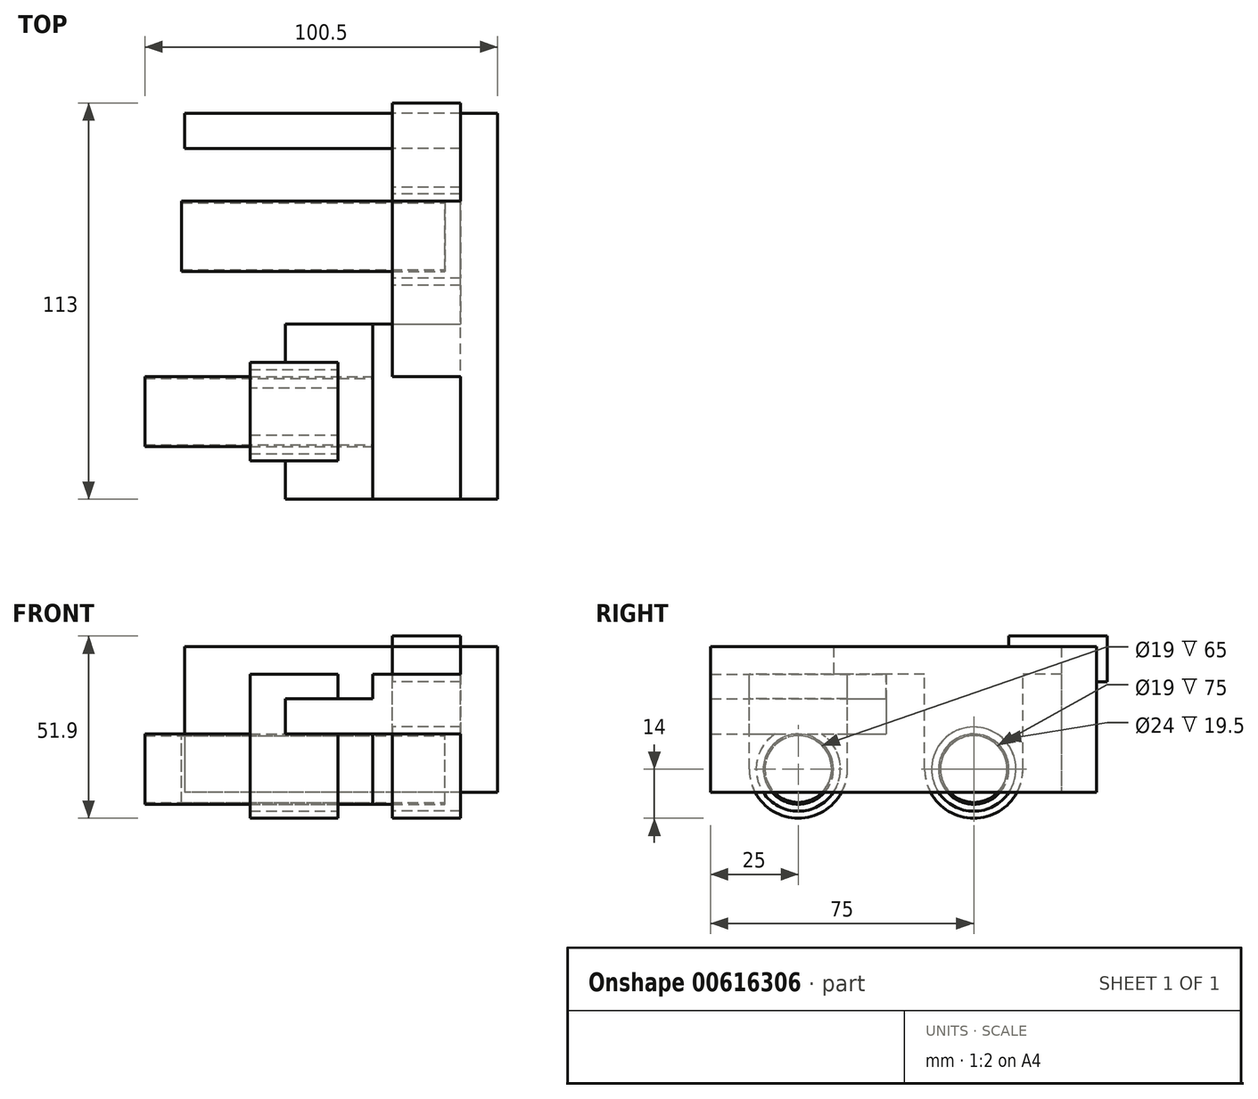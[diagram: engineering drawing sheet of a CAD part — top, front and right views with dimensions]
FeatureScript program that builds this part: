
annotation { "Feature Type Name" : "Feature", "Feature Type Description" : "" }
export const myFeature = defineFeature(function(context is Context, id is Id, definition is map)
    precondition{}
    {
        {
            var Q0;
            Q0=qCreatedBy(makeId("Front.planeOp"),FACE);
            var sketch = newSketch(context, id + "F0", { "sketchPlane" : qUnion([Q0])});
            skLineSegment(sketch, "E0.bottom", {"start": v(-30.5, 5.1) * mm, "end": v(30, 5.1) * mm});
            skLineSegment(sketch, "E0.top", {"start": v(-30.5, -5) * mm, "end": v(30, -5) * mm});
            skLineSegment(sketch, "E0.left", {"start": v(-30.5, 5.1) * mm, "end": v(-30.5, -5) * mm});
            skPoint(sketch, "E0.middle", {"position": v(0, 0) * mm});
            skLineSegment(sketch, "E1.bottom", {"start": v(-5.5, 5.1) * mm, "end": v(30, 5.1) * mm});
            skLineSegment(sketch, "E1.top", {"start": v(-5.5, 12.1) * mm, "end": v(30, 12.1) * mm});
            skLineSegment(sketch, "E1.left", {"start": v(-5.5, 5.1) * mm, "end": v(-5.5, 12.1) * mm});
            skLineSegment(sketch, "E2", {"start": v(19.5, 5.1) * mm, "end": v(19.5, 12.1) * mm});
            skLineSegment(sketch, "E3", {"start": v(30, -5) * mm, "end": v(30, 19.9) * mm});
            skLineSegment(sketch, "E4", {"start": v(30, 19.9) * mm, "end": v(19.5, 19.9) * mm});
            skLineSegment(sketch, "E5", {"start": v(19.5, 19.9) * mm, "end": v(19.5, -5) * mm});
            skLineSegment(sketch, "E6.bottom", {"start": v(19.5, -5) * mm, "end": v(30, -5) * mm});
            skLineSegment(sketch, "E6.top", {"start": v(19.5, -21.67) * mm, "end": v(30, -21.67) * mm});
            skLineSegment(sketch, "E6.left", {"start": v(19.5, -5) * mm, "end": v(19.5, -21.67) * mm});
            skLineSegment(sketch, "E6.right", {"start": v(30, -5) * mm, "end": v(30, -21.67) * mm});
            skSolve(sketch);
        }
        {
            var Q0;
            {var subQ0=sQuery(id+"F0.wireOp",EDGE,"E0.left");var subQ5=sQuery(id+"F0.wireOp",EDGE,"E2");var subQ6=sQuery(id+"F0.wireOp",EDGE,"E0.bottom");var subQ9=sQuery(id+"F0.wireOp",EDGE,"E1.left");var subQ12=sQuery(id+"F0.wireOp",EDGE,"E3");var subQ13=makeQuery(id+"F0.imprint","INTERSECT",VERTEX,{"derivedFrom":[subQ6,subQ12]});var subQ14=makeQuery(id+"F0.imprint","IMPRINT",EDGE,{"disambiguationData":[TD([[subQ13,1.0]])],"derivedFrom":subQ6});var subQ19=makeQuery(id+"F0.imprint","IMPRINT",EDGE,{"derivedFrom":subQ5});var subQ20=sQuery(id+"F0.wireOp",EDGE,"E4");Q0=qUnion([makeQuery(id+"F0.imprint","IMPRINT",FACE,{"disambiguationData":[TD([[makeQuery(id+"F0.imprint","IMPRINT",EDGE,{"derivedFrom":subQ9}),-1.0]])]}),makeQuery(id+"F0.imprint","IMPRINT",FACE,{"disambiguationData":[TD([[makeQuery(id+"F0.imprint","IMPRINT",EDGE,{"derivedFrom":sQuery(id+"F0.wireOp",EDGE,"E6.top")}),1.0]])]}),makeQuery(id+"F0.imprint","IMPRINT",FACE,{"disambiguationData":[TD([[subQ14,-1.0]])]}),makeQuery(id+"F0.imprint","IMPRINT",FACE,{"disambiguationData":[TD([[makeQuery(id+"F0.imprint","IMPRINT",EDGE,{"derivedFrom":subQ20}),1.0]])]}),makeQuery(id+"F0.imprint","IMPRINT",FACE,{"disambiguationData":[TD([[subQ19,-1.0]])]}),makeQuery(id+"F0.imprint","IMPRINT",FACE,{"disambiguationData":[TD([[makeQuery(id+"F0.imprint","IMPRINT",EDGE,{"derivedFrom":subQ0}),1.0]])]})]);}
            extrude(context, id + "F1", {"entities" : qUnion([Q0]), "depth" : 25 * mm, "offsetDistance" : 25 * mm, "hasSecondDirection" : true, "secondDirectionOppositeDirection" : true, "secondDirectionDepth" : 25 * mm});
        }
        {
            var Q0;
            Q0=makeQuery(id+"F1.opExtrude","CAP_FACE",FACE,{"disambiguationData":[OSD([sQuery(id+"F0.wireOp",EDGE,"E0.bottom"),sQuery(id+"F0.wireOp",EDGE,"E0.top"),sQuery(id+"F0.wireOp",EDGE,"E0.left"),sQuery(id+"F0.wireOp",EDGE,"E1.top"),sQuery(id+"F0.wireOp",EDGE,"E1.left"),sQuery(id+"F0.wireOp",EDGE,"E3"),sQuery(id+"F0.wireOp",EDGE,"E4"),sQuery(id+"F0.wireOp",EDGE,"E5"),sQuery(id+"F0.wireOp",EDGE,"E6.top"),sQuery(id+"F0.wireOp",EDGE,"E6.left"),sQuery(id+"F0.wireOp",EDGE,"E6.right")])],"isStart":true});
            var sketch = newSketch(context, id + "F2", { "sketchPlane" : qUnion([Q0])});
            skLineSegment(sketch, "E7.0.0", {"start": v(-19.5, 12.1) * mm, "end": v(-19.5, 19.9) * mm, "construction": true});
            skLineSegment(sketch, "E7.0.1", {"start": v(-19.5, 19.9) * mm, "end": v(-30, 19.9) * mm, "construction": true});
            skLineSegment(sketch, "E7.0.2", {"start": v(-30, 19.9) * mm, "end": v(-30, -21.67) * mm, "construction": true});
            skLineSegment(sketch, "E7.0.3", {"start": v(-30, -21.67) * mm, "end": v(-19.5, -21.67) * mm, "construction": true});
            skLineSegment(sketch, "E7.0.4", {"start": v(-19.5, -21.67) * mm, "end": v(-19.5, -5) * mm, "construction": true});
            skLineSegment(sketch, "E7.0.5", {"start": v(-19.5, -5) * mm, "end": v(30.5, -5) * mm, "construction": true});
            skLineSegment(sketch, "E7.0.6", {"start": v(30.5, -5) * mm, "end": v(30.5, 5.1) * mm, "construction": true});
            skLineSegment(sketch, "E7.0.7", {"start": v(30.5, 5.1) * mm, "end": v(5.5, 5.1) * mm, "construction": true});
            skLineSegment(sketch, "E7.0.8", {"start": v(5.5, 5.1) * mm, "end": v(5.5, 12.1) * mm, "construction": true});
            skLineSegment(sketch, "E7.0.9", {"start": v(5.5, 12.1) * mm, "end": v(-19.5, 12.1) * mm, "construction": true});
            skLineSegment(sketch, "E8.bottom", {"start": v(-30, 19.9) * mm, "end": v(-19.5, 19.9) * mm});
            skLineSegment(sketch, "E8.top", {"start": v(-30, -21.67) * mm, "end": v(-19.5, -21.67) * mm});
            skLineSegment(sketch, "E8.left", {"start": v(-30, 19.9) * mm, "end": v(-30, -21.67) * mm});
            skLineSegment(sketch, "E8.right", {"start": v(-19.5, 19.9) * mm, "end": v(-19.5, -21.67) * mm});
            skSolve(sketch);
        }
        {
            var Q0;
            Q0 = qSketchRegion(id + "F2", true);
            extrude(context, id + "F3", {"entities" : qUnion([Q0]), "operationType" : NewBodyOperationType.ADD, "depth" : 50 * mm, "offsetDistance" : 25 * mm});
        }
        {
            var Q0;
            Q0=makeQuery(id+"F3.opExtrude","CAP_FACE",FACE,{"disambiguationData":[OSD([sQuery(id+"F2.wireOp",EDGE,"E8.bottom"),sQuery(id+"F2.wireOp",EDGE,"E8.top"),sQuery(id+"F2.wireOp",EDGE,"E8.left"),sQuery(id+"F2.wireOp",EDGE,"E8.right")])],"isStart":false});
            var sketch = newSketch(context, id + "F4", { "sketchPlane" : qUnion([Q0])});
            skLineSegment(sketch, "E9.0.0", {"start": v(-19.5, -21.67) * mm, "end": v(-19.5, 19.9) * mm, "construction": true});
            skLineSegment(sketch, "E9.0.1", {"start": v(-19.5, 19.9) * mm, "end": v(-30, 19.9) * mm, "construction": true});
            skLineSegment(sketch, "E9.0.2", {"start": v(-30, 19.9) * mm, "end": v(-30, -21.67) * mm, "construction": true});
            skLineSegment(sketch, "E9.0.3", {"start": v(-30, -21.67) * mm, "end": v(-19.5, -21.67) * mm, "construction": true});
            skLineSegment(sketch, "E10.bottom", {"start": v(-30, 19.9) * mm, "end": v(59.17, 19.9) * mm});
            skLineSegment(sketch, "E10.top", {"start": v(-30, -21.67) * mm, "end": v(59.17, -21.67) * mm});
            skLineSegment(sketch, "E10.left", {"start": v(-30, 19.9) * mm, "end": v(-30, -21.67) * mm});
            skLineSegment(sketch, "E10.right", {"start": v(59.17, 19.9) * mm, "end": v(59.17, -21.67) * mm});
            skSolve(sketch);
        }
        {
            var Q0;
            Q0 = qSketchRegion(id + "F4", true);
            extrude(context, id + "F5", {"entities" : qUnion([Q0]), "operationType" : NewBodyOperationType.ADD, "depth" : 10 * mm, "offsetDistance" : 25 * mm});
        }
        {
            var Q0;
            Q0=makeQuery(id+"F1.opExtrude","SWEPT_FACE",FACE,{"disambiguationData":[OSD([sQuery(id+"F0.wireOp",EDGE,"E0.left")])]});
            var sketch = newSketch(context, id + "F6", { "sketchPlane" : qUnion([Q0])});
            skPoint(sketch, "E11", {"position": v(0, -15) * mm});
            skLineSegment(sketch, "E12.0", {"start": v(25, -5) * mm, "end": v(-25, -5) * mm, "construction": true});
            skCircle(sketch, "E13", {"center": v(0, -15) * mm, "radius": 10 * mm});
            skCircle(sketch, "E14", {"center": v(0, -15) * mm, "radius": 9.5 * mm});
            skSolve(sketch);
        }
        {
            var Q0;
            Q0=qSketchRegion(id+"F6",true);
            extrude(context, id + "F7", {"entities" : qUnion([Q0]), "depth" : 40 * mm, "offsetDistance" : 25 * mm, "hasSecondDirection" : true, "secondDirectionOppositeDirection" : true, "secondDirectionDepth" : 25 * mm});
        }
        {
            var Q0;
            Q0=makeQuery(id+"F1.opExtrude","SWEPT_FACE",FACE,{"disambiguationData":[OSD([sQuery(id+"F0.wireOp",EDGE,"E0.left")])]});
            var sketch = newSketch(context, id + "F8", { "sketchPlane" : qUnion([Q0])});
            skCircle(sketch, "E15.0", {"center": v(0, -15) * mm, "radius": 10 * mm, "construction": true});
            skLineSegment(sketch, "E16.0", {"start": v(25, -5) * mm, "end": v(-25, -5) * mm, "construction": true});
            skLineSegment(sketch, "E17.0", {"start": v(25, 5.1) * mm, "end": v(-25, 5.1) * mm, "construction": true});
            skCircle(sketch, "E18", {"center": v(0, -15) * mm, "radius": 12 * mm});
            skCircle(sketch, "E19", {"center": v(0, -15) * mm, "radius": 14 * mm});
            skLineSegment(sketch, "E20", {"start": v(0, -15) * mm, "end": v(20.33, -15) * mm, "construction": true});
            skLineSegment(sketch, "E21", {"start": v(14, -15) * mm, "end": v(14, -5) * mm});
            skLineSegment(sketch, "E22", {"start": v(-14, -15) * mm, "end": v(-14, -5) * mm});
            skLineSegment(sketch, "E23", {"start": v(-14, -5) * mm, "end": v(14, -5) * mm});
            skLineSegment(sketch, "E24", {"start": v(-14, -5) * mm, "end": v(-14, 5.1) * mm});
            skLineSegment(sketch, "E25", {"start": v(-14, 5.1) * mm, "end": v(14, 5.1) * mm});
            skLineSegment(sketch, "E26", {"start": v(14, 5.1) * mm, "end": v(14, -5) * mm});
            skLineSegment(sketch, "E27.0", {"start": v(25, 12.1) * mm, "end": v(-25, 12.1) * mm, "construction": true});
            skLineSegment(sketch, "E28", {"start": v(-14, 5.1) * mm, "end": v(-14, 12.1) * mm});
            skLineSegment(sketch, "E29", {"start": v(-14, 12.1) * mm, "end": v(14, 12.1) * mm});
            skLineSegment(sketch, "E30", {"start": v(14, 12.1) * mm, "end": v(14, 5.1) * mm});
            skSolve(sketch);
        }
        {
            var Q0;
            {var subQ3=sQuery(id+"F8.wireOp",EDGE,"E23");var subQ6=sQuery(id+"F8.wireOp",EDGE,"E18");var subQ7=makeQuery(id+"F8.imprint","INTERSECT",VERTEX,{"disambiguationData":[OD(0.0)],"derivedFrom":[subQ6,subQ3]});Q0=makeQuery(id+"F8.imprint","IMPRINT",FACE,{"disambiguationData":[TD([[makeQuery(id+"F8.imprint","IMPRINT",EDGE,{"disambiguationData":[TD([[subQ7,1.0]])],"derivedFrom":subQ6}),-1.0]])]});}
            var Q1;
            {var subQ0=sQuery(id+"F8.wireOp",EDGE,"E22");Q1=makeQuery(id+"F8.imprint","IMPRINT",FACE,{"disambiguationData":[TD([[makeQuery(id+"F8.imprint","IMPRINT",EDGE,{"derivedFrom":subQ0}),-1.0]])]});}
            var Q2;
            {var subQ0=sQuery(id+"F8.wireOp",EDGE,"E21");Q2=makeQuery(id+"F8.imprint","IMPRINT",FACE,{"disambiguationData":[TD([[makeQuery(id+"F8.imprint","IMPRINT",EDGE,{"derivedFrom":subQ0}),1.0]])]});}
            var Q3;
            {var subQ0=sQuery(id+"F8.wireOp",EDGE,"E24");Q3=makeQuery(id+"F8.imprint","IMPRINT",FACE,{"disambiguationData":[TD([[makeQuery(id+"F8.imprint","IMPRINT",EDGE,{"derivedFrom":subQ0}),-1.0]])]});}
            var Q4;
            {var subQ0=sQuery(id+"F8.wireOp",EDGE,"E23");var subQ1=sQuery(id+"F8.wireOp",EDGE,"E18");var subQ2=makeQuery(id+"F8.imprint","INTERSECT",VERTEX,{"disambiguationData":[OD(0.0)],"derivedFrom":[subQ1,subQ0]});Q4=makeQuery(id+"F8.imprint","IMPRINT",FACE,{"disambiguationData":[TD([[makeQuery(id+"F8.imprint","IMPRINT",EDGE,{"disambiguationData":[TD([[subQ2,-1.0]])],"derivedFrom":subQ1}),-1.0]])]});}
            var Q5;
            {var subQ0=sQuery(id+"F8.wireOp",EDGE,"E23");var subQ1=sQuery(id+"F8.wireOp",EDGE,"E18");var subQ2=makeQuery(id+"F8.imprint","INTERSECT",VERTEX,{"disambiguationData":[OD(0.0)],"derivedFrom":[subQ1,subQ0]});Q5=makeQuery(id+"F8.imprint","IMPRINT",FACE,{"disambiguationData":[TD([[makeQuery(id+"F8.imprint","IMPRINT",EDGE,{"disambiguationData":[TD([[subQ2,-1.0]])],"derivedFrom":subQ1}),1.0]])]});}
            var Q6;
            Q6=makeQuery(id+"F8.imprint","IMPRINT",FACE,{"disambiguationData":[TD([[makeQuery(id+"F8.imprint","IMPRINT",EDGE,{"derivedFrom":sQuery(id+"F8.wireOp",EDGE,"E25")}),-1.0]])]});
            extrude(context, id + "F9", {"entities" : qUnion([Q0, Q1, Q2, Q3, Q4, Q5, Q6]), "depth" : 10 * mm, "offsetDistance" : 25 * mm});
        }
        {
            var Q0;
            Q0=makeQuery(id+"F9.opExtrude","CAP_FACE",FACE,{"disambiguationData":[OSD([sQuery(id+"F8.wireOp",EDGE,"E18"),sQuery(id+"F8.wireOp",EDGE,"E19"),sQuery(id+"F8.wireOp",EDGE,"E21"),sQuery(id+"F8.wireOp",EDGE,"E22"),sQuery(id+"F8.wireOp",EDGE,"E23"),sQuery(id+"F8.wireOp",EDGE,"E24"),sQuery(id+"F8.wireOp",EDGE,"E26"),sQuery(id+"F8.wireOp",EDGE,"E28"),sQuery(id+"F8.wireOp",EDGE,"E29"),sQuery(id+"F8.wireOp",EDGE,"E30")])],"isStart":true});
            var sketch = newSketch(context, id + "F10", { "sketchPlane" : qUnion([Q0])});
            skLineSegment(sketch, "E31.0", {"start": v(-25, 12.1) * mm, "end": v(25, 12.1) * mm, "construction": true});
            skLineSegment(sketch, "E32.0", {"start": v(-25, 5.1) * mm, "end": v(25, 5.1) * mm, "construction": true});
            skLineSegment(sketch, "E33.0", {"start": v(14, -15) * mm, "end": v(14, 12.1) * mm, "construction": true});
            skLineSegment(sketch, "E34.0", {"start": v(-14, -15) * mm, "end": v(-14, 12.1) * mm, "construction": true});
            skLineSegment(sketch, "E35.bottom", {"start": v(14, 12.1) * mm, "end": v(-14, 12.1) * mm});
            skLineSegment(sketch, "E35.top", {"start": v(14, 5.1) * mm, "end": v(-14, 5.1) * mm});
            skLineSegment(sketch, "E35.left", {"start": v(14, 12.1) * mm, "end": v(14, 5.1) * mm});
            skLineSegment(sketch, "E35.right", {"start": v(-14, 12.1) * mm, "end": v(-14, 5.1) * mm});
            skArc(sketch, "E36.0", {"start": v(6.63, -5) * mm, "mid": v(0, -27) * mm, "end": v(-6.63, -5) * mm});
            skLineSegment(sketch, "E37.0", {"start": v(-25, -5) * mm, "end": v(25, -5) * mm, "construction": true});
            skPoint(sketch, "E38.0", {"position": v(14, -15) * mm});
            skPoint(sketch, "E39.0", {"position": v(-14, -15) * mm});
            skArc(sketch, "E40.0", {"start": v(14, -15) * mm, "mid": v(0, -29) * mm, "end": v(-14, -15) * mm});
            skArc(sketch, "E41.0.0", {"start": v(-14, -15) * mm, "mid": v(0, -29) * mm, "end": v(14, -15) * mm, "construction": true});
            skLineSegment(sketch, "E41.0.2", {"start": v(14, 12.1) * mm, "end": v(-14, 12.1) * mm, "construction": true});
            skLineSegment(sketch, "E41.0.3", {"start": v(-14, 12.1) * mm, "end": v(-14, -15) * mm, "construction": true});
            skLineSegment(sketch, "E42", {"start": v(-14, -15) * mm, "end": v(-14, -5) * mm});
            skLineSegment(sketch, "E43", {"start": v(-14, -5) * mm, "end": v(14, -5) * mm});
            skLineSegment(sketch, "E44", {"start": v(14, -5) * mm, "end": v(14, -15) * mm});
            skSolve(sketch);
        }
        {
            var Q0;
            Q0=makeQuery(id+"F10.imprint","IMPRINT",FACE,{"disambiguationData":[TD([[makeQuery(id+"F10.imprint","IMPRINT",EDGE,{"derivedFrom":sQuery(id+"F10.wireOp",EDGE,"E35.bottom")}),1.0]])]});
            var Q1;
            {var subQ1=sQuery(id+"F10.wireOp",EDGE,"E36.0");Q1=makeQuery(id+"F10.imprint","IMPRINT",FACE,{"disambiguationData":[TD([[makeQuery(id+"F10.imprint","IMPRINT",EDGE,{"derivedFrom":subQ1}),1.0]])]});}
            extrude(context, id + "F11", {"entities" : qUnion([Q0, Q1]), "operationType" : NewBodyOperationType.ADD, "depth" : 15 * mm, "offsetDistance" : 25 * mm});
        }
        {
            var Q0;
            Q0=qCreatedBy(makeId("Right.planeOp"),FACE);
            var sketch = newSketch(context, id + "F12", { "sketchPlane" : qUnion([Q0])});
            skLineSegment(sketch, "E45", {"start": v(0, 0) * mm, "end": v(71.15, 0) * mm, "construction": true});
            skCircle(sketch, "E46.0", {"center": v(0, -15) * mm, "radius": 9.5 * mm, "construction": true});
            skCircle(sketch, "E47.0", {"center": v(0, -15) * mm, "radius": 10 * mm, "construction": true});
            skLineSegment(sketch, "E48", {"start": v(0, -15) * mm, "end": v(68.73, -15) * mm, "construction": true});
            skLineSegment(sketch, "E49.0", {"start": v(75, 19.9) * mm, "end": v(75, -21.67) * mm, "construction": true});
            skLineSegment(sketch, "E50.0", {"start": v(25, 5.1) * mm, "end": v(25, -5) * mm, "construction": true});
            skCircle(sketch, "E51", {"center": v(50, -15) * mm, "radius": 9.5 * mm});
            skCircle(sketch, "E52", {"center": v(50, -15) * mm, "radius": 10 * mm});
            skSolve(sketch);
        }
        {
            var Q0;
            Q0 = qSketchRegion(id + "F12", true);
            extrude(context, id + "F13", {"entities" : qUnion([Q0]), "oppositeDirection" : true, "depth" : 60 * mm, "offsetDistance" : 25 * mm, "hasSecondDirection" : true, "secondDirectionOppositeDirection" : false, "secondDirectionDepth" : 15 * mm});
        }
        {
            var Q0;
            Q0=qCreatedBy(makeId("Right.planeOp"),FACE);
            var sketch = newSketch(context, id + "F14", { "sketchPlane" : qUnion([Q0])});
            skCircle(sketch, "E53.0", {"center": v(50, -15) * mm, "radius": 9.5 * mm});
            skCircle(sketch, "E54.0", {"center": v(50, -15) * mm, "radius": 10 * mm});
            skCircle(sketch, "E55", {"center": v(50, -15) * mm, "radius": 12 * mm});
            skCircle(sketch, "E56", {"center": v(50, -15) * mm, "radius": 14 * mm});
            skLineSegment(sketch, "E57.0", {"start": v(-25, 12.1) * mm, "end": v(25, 12.1) * mm, "construction": true});
            skLineSegment(sketch, "E58.0", {"start": v(75, 19.9) * mm, "end": v(75, -21.67) * mm, "construction": true});
            skLineSegment(sketch, "E59", {"start": v(36, -15) * mm, "end": v(36, 12.1) * mm});
            skLineSegment(sketch, "E60", {"start": v(64, -15) * mm, "end": v(64, 12.1) * mm});
            skLineSegment(sketch, "E61", {"start": v(64, 12.1) * mm, "end": v(36, 12.1) * mm});
            skLineSegment(sketch, "E62.bottom", {"start": v(75, 19.9) * mm, "end": v(10, 19.9) * mm});
            skLineSegment(sketch, "E62.top", {"start": v(75, 12.1) * mm, "end": v(10, 12.1) * mm});
            skLineSegment(sketch, "E62.left", {"start": v(75, 19.9) * mm, "end": v(75, 12.1) * mm});
            skLineSegment(sketch, "E62.right", {"start": v(10, 19.9) * mm, "end": v(10, 12.1) * mm});
            skSolve(sketch);
        }
        {
            var Q0;
            {var subQ0=sQuery(id+"F14.wireOp",EDGE,"E59");var subQ6=sQuery(id+"F14.wireOp",EDGE,"E61");var subQ7=makeQuery(id+"F14.imprint","IMPRINT",EDGE,{"derivedFrom":subQ6});Q0=qUnion([makeQuery(id+"F14.imprint","IMPRINT",FACE,{"disambiguationData":[TD([[subQ7,-1.0]])]}),makeQuery(id+"F14.imprint","IMPRINT",FACE,{"disambiguationData":[TD([[makeQuery(id+"F14.imprint","IMPRINT",EDGE,{"derivedFrom":sQuery(id+"F14.wireOp",EDGE,"E55")}),-1.0]])]}),makeQuery(id+"F14.imprint","IMPRINT",FACE,{"disambiguationData":[TD([[makeQuery(id+"F14.imprint","IMPRINT",EDGE,{"derivedFrom":subQ0}),-1.0]])]})]);}
            var Q1;
            Q1=makeQuery(id+"F3.boolean.opBoolean","MERGE",FACE,{"derivedFrom":[makeQuery(id+"F1.opExtrude","SWEPT_FACE",FACE,{"disambiguationData":[OSD([sQuery(id+"F0.wireOp",EDGE,"E5")])]}),makeQuery(id+"F1.opExtrude","SWEPT_FACE",FACE,{"disambiguationData":[OSD([sQuery(id+"F0.wireOp",EDGE,"E6.left")])]}),makeQuery(id+"F3.opExtrude","SWEPT_FACE",FACE,{"disambiguationData":[OSD([sQuery(id+"F2.wireOp",EDGE,"E8.right")])]})]});
            extrude(context, id + "F15", {"entities" : qUnion([Q0]), "endBound" : BoundingType.UP_TO_SURFACE, "depth" : 10 * mm, "endBoundEntityFace" : qUnion([Q1]), "offsetDistance" : 25 * mm});
        }
        {
            var Q0;
            Q0=makeQuery(id+"F15.opExtrude","SWEPT_FACE",FACE,{"disambiguationData":[OSD([sQuery(id+"F14.wireOp",EDGE,"E62.bottom")])]});
            var sketch = newSketch(context, id + "F16", { "sketchPlane" : qUnion([Q0])});
            skLineSegment(sketch, "E63.0.0", {"start": v(19.5, 10) * mm, "end": v(19.5, 75) * mm, "construction": true});
            skLineSegment(sketch, "E63.0.1", {"start": v(19.5, 75) * mm, "end": v(0, 75) * mm, "construction": true});
            skLineSegment(sketch, "E63.0.2", {"start": v(0, 75) * mm, "end": v(0, 10) * mm, "construction": true});
            skLineSegment(sketch, "E63.0.3", {"start": v(0, 10) * mm, "end": v(19.5, 10) * mm, "construction": true});
            skLineSegment(sketch, "E64.0.0", {"start": v(30, -25) * mm, "end": v(30, 85) * mm, "construction": true});
            skLineSegment(sketch, "E64.0.1", {"start": v(30, 85) * mm, "end": v(-59.17, 85) * mm, "construction": true});
            skLineSegment(sketch, "E64.0.2", {"start": v(-59.17, 85) * mm, "end": v(-59.17, 75) * mm, "construction": true});
            skLineSegment(sketch, "E64.0.3", {"start": v(-59.17, 75) * mm, "end": v(19.5, 75) * mm, "construction": true});
            skLineSegment(sketch, "E64.0.4", {"start": v(19.5, 75) * mm, "end": v(19.5, -25) * mm, "construction": true});
            skLineSegment(sketch, "E64.0.5", {"start": v(19.5, -25) * mm, "end": v(30, -25) * mm, "construction": true});
            skLineSegment(sketch, "E65", {"start": v(15, 40) * mm, "end": v(-60, 40) * mm, "construction": true});
            skLineSegment(sketch, "E66", {"start": v(-60, 60) * mm, "end": v(15, 60) * mm, "construction": true});
            skPoint(sketch, "E67", {"position": v(0, 60) * mm});
            skLineSegment(sketch, "E68.bottom", {"start": v(0, 60) * mm, "end": v(19.5, 60) * mm});
            skLineSegment(sketch, "E68.top", {"start": v(0, 85) * mm, "end": v(19.5, 85) * mm});
            skLineSegment(sketch, "E68.left", {"start": v(0, 60) * mm, "end": v(0, 85) * mm});
            skLineSegment(sketch, "E68.right", {"start": v(19.5, 60) * mm, "end": v(19.5, 85) * mm});
            skSolve(sketch);
        }
        {
            var Q0;
            Q0 = qSketchRegion(id + "F16", true);
            extrude(context, id + "F17", {"entities" : qUnion([Q0]), "operationType" : NewBodyOperationType.ADD, "depth" : 3 * mm, "offsetDistance" : 25 * mm});
        }
        {
            var Q0;
            Q0=makeQuery(id+"F17.opExtrude","SWEPT_FACE",FACE,{"disambiguationData":[OSD([sQuery(id+"F16.wireOp",EDGE,"E68.top")])]});
            var sketch = newSketch(context, id + "F18", { "sketchPlane" : qUnion([Q0])});
            skLineSegment(sketch, "E69.0.0", {"start": v(-19.5, 19.9) * mm, "end": v(0, 19.9) * mm, "construction": true});
            skLineSegment(sketch, "E69.0.1", {"start": v(0, 19.9) * mm, "end": v(0, 22.9) * mm, "construction": true});
            skLineSegment(sketch, "E69.0.2", {"start": v(0, 22.9) * mm, "end": v(-19.5, 22.9) * mm, "construction": true});
            skLineSegment(sketch, "E69.0.3", {"start": v(-19.5, 22.9) * mm, "end": v(-19.5, 19.9) * mm, "construction": true});
            skLineSegment(sketch, "E70.bottom", {"start": v(-19.5, 22.9) * mm, "end": v(0, 22.9) * mm});
            skLineSegment(sketch, "E70.top", {"start": v(-19.5, 9.9) * mm, "end": v(0, 9.9) * mm});
            skLineSegment(sketch, "E70.left", {"start": v(-19.5, 22.9) * mm, "end": v(-19.5, 9.9) * mm});
            skLineSegment(sketch, "E70.right", {"start": v(0, 22.9) * mm, "end": v(0, 9.9) * mm});
            skSolve(sketch);
        }
        {
            var Q0;
            Q0 = qSketchRegion(id + "F18", true);
            extrude(context, id + "F19", {"entities" : qUnion([Q0]), "operationType" : NewBodyOperationType.ADD, "depth" : 3 * mm, "offsetDistance" : 25 * mm});
        }
    });
